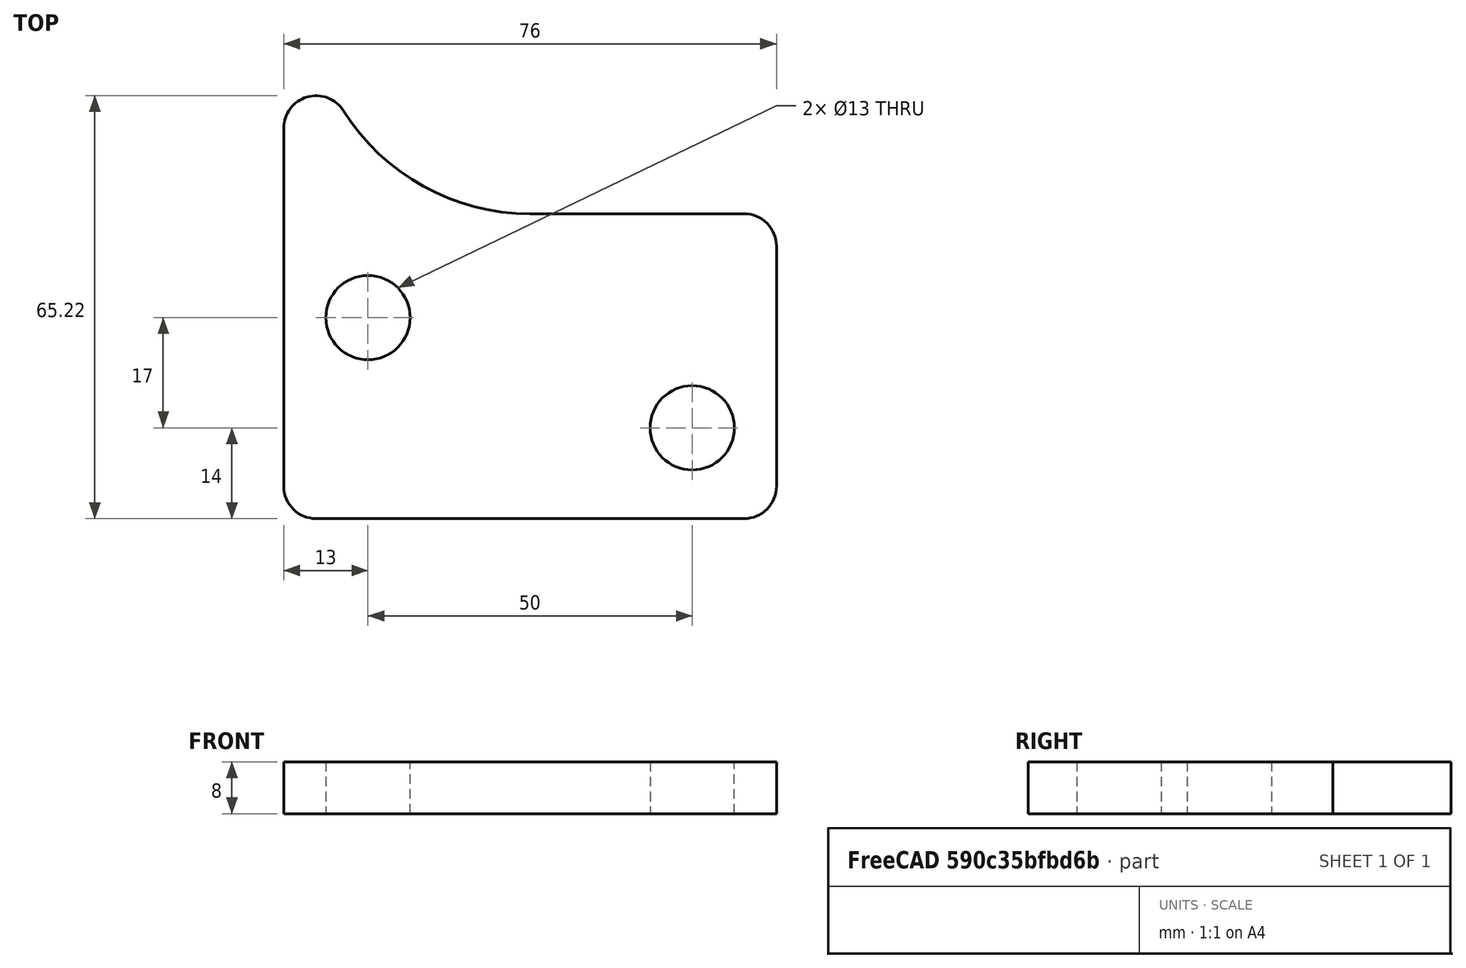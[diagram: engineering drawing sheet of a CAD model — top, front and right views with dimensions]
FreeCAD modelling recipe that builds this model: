
FCSTD DOCUMENT  (FreeCAD 0.19R24366 (Git))
Label: Actuator location plate
License: All rights reserved
LicenseURL: http://en.wikipedia.org/wiki/All_rights_reserved
objects: Sketcher::SketchObject×1, PartDesign::Pad×1, PartDesign::Body×1
note: 4 computed .brp shape members not serialized (recipe doc carries the construction recipe); baked Part::Feature solids carry a one-line shape summary decoded from their .brp

FEATURE [Sketcher::SketchObject] Sketch
  FullyConstrained = true
  MapMode = 5
  Support = -> [XY_Plane]
  sketch-geometry (17):
    g0: Circle CenterX=0 CenterY=0 CenterZ=0 NormalX=0 NormalY=0 NormalZ=1 AngleXU=0 Radius=15
    g1: Circle CenterX=0 CenterY=0 CenterZ=0 NormalX=0 NormalY=0 NormalZ=1 AngleXU=0 Radius=32
    g2: Circle CenterX=0 CenterY=0 CenterZ=0 NormalX=0 NormalY=0 NormalZ=1 AngleXU=0 Radius=40
    g3: ArcOfCircle CenterX=0 CenterY=0 CenterZ=0 NormalX=0 NormalY=0 NormalZ=1 AngleXU=0 Radius=34 StartAngle=3.70366 EndAngle=4.71239
    g4: LineSegment StartX=-6.2e-15 StartY=-34 StartZ=0 EndX=33 EndY=-34 EndZ=0
    g5: GeomPoint X=0 Y=-100 Z=0
    g6: LineSegment StartX=-38 StartY=-20.7846 StartZ=0 EndX=-38 EndY=-76 EndZ=0
    g7: LineSegment StartX=38 StartY=-39 StartZ=0 EndX=38 EndY=-76 EndZ=0
    g8: LineSegment StartX=-33 StartY=-81 StartZ=0 EndX=33 EndY=-81 EndZ=0
    g9: ArcOfCircle CenterX=-33 CenterY=-20.7846 CenterZ=0 NormalX=0 NormalY=0 NormalZ=1 AngleXU=0 Radius=5 StartAngle=0.56207 EndAngle=3.14159
    g10: ArcOfCircle CenterX=33 CenterY=-39 CenterZ=0 NormalX=0 NormalY=0 NormalZ=1 AngleXU=0 Radius=5 StartAngle=-9e-16 EndAngle=1.5708
    g11: ArcOfCircle CenterX=33 CenterY=-76 CenterZ=0 NormalX=0 NormalY=0 NormalZ=1 AngleXU=0 Radius=5 StartAngle=4.71239 EndAngle=6.28319
    g12: ArcOfCircle CenterX=-33 CenterY=-76 CenterZ=0 NormalX=0 NormalY=0 NormalZ=1 AngleXU=0 Radius=5 StartAngle=3.14159 EndAngle=4.71239
    g13: Circle CenterX=-25 CenterY=-50 CenterZ=0 NormalX=0 NormalY=0 NormalZ=1 AngleXU=0 Radius=6.5
    g14: Circle CenterX=-25 CenterY=-50 CenterZ=0 NormalX=0 NormalY=0 NormalZ=1 AngleXU=0 Radius=12
    g15: Circle CenterX=25 CenterY=-67 CenterZ=0 NormalX=0 NormalY=0 NormalZ=1 AngleXU=0 Radius=6.5
    g16: Circle CenterX=25 CenterY=-67 CenterZ=0 NormalX=0 NormalY=0 NormalZ=1 AngleXU=0 Radius=12
  constraints (41):
    c: Coincident(g0,g-1)
    c: Coincident(g1,g0)
    c: Coincident(g2,g0)
    c: Radius(g0) = 15
    c: Radius(g1) = 32
    c: Radius(g2) = 40
    c: Coincident(g3,g0)
    c: PointOnObject(g3,g-2)
    c: Radius(g3) = 34
    c: Coincident(g4,g3)
    c: Horizontal(g4)
    c: PointOnObject(g5,g-2)
    c: DistanceY(g5,g0) = 100
    c: Vertical(g6)
    c: Vertical(g7)
    c: Tangent(g3,g9) = 1.5708
    c: Tangent(g6,g9) = -1.5708
    c: Tangent(g4,g10) = 1.5708
    c: Tangent(g7,g10) = 1.5708
    c: Tangent(g7,g11) = 1.5708
    c: Tangent(g8,g11) = -1.5708
    c: Tangent(g8,g12) = -1.5708
    c: Tangent(g6,g12) = -1.5708
    c: Symmetric(g8,g8,g-2)
    c: Equal(g11,g10)
    c: Equal(g10,g9)
    c: Angle(g3) = 1.00873
    c: Equal(g12,g9)
    c: Radius(g11) = 5
    c: DistanceY(g5,g8) = 19
    c: Coincident(g14,g13)
    c: Coincident(g16,g15)
    c: Equal(g15,g13)
    c: Radius(g15) = 6.5
    c: Radius(g16) = 12
    c: Equal(g14,g16)
    c: DistanceX(g13,g-1) = 25
    c: DistanceX(g3,g15) = 25
    c: DistanceY(g8,g15) = 14
    c: DistanceY(g15,g13) = 17
    c: DistanceX(g6,g7) = 76
FEATURE [PartDesign::Pad] Pad  label="8mm thick plate"
  Direction = (1,1,1)
  Length = 8
  Length2 = 100
  Profile = -> Sketch
  Type = 0
FEATURE [PartDesign::Body] Body
  Group = -> [Sketch,Pad]
  Origin = -> Origin
  Tip = -> Pad
